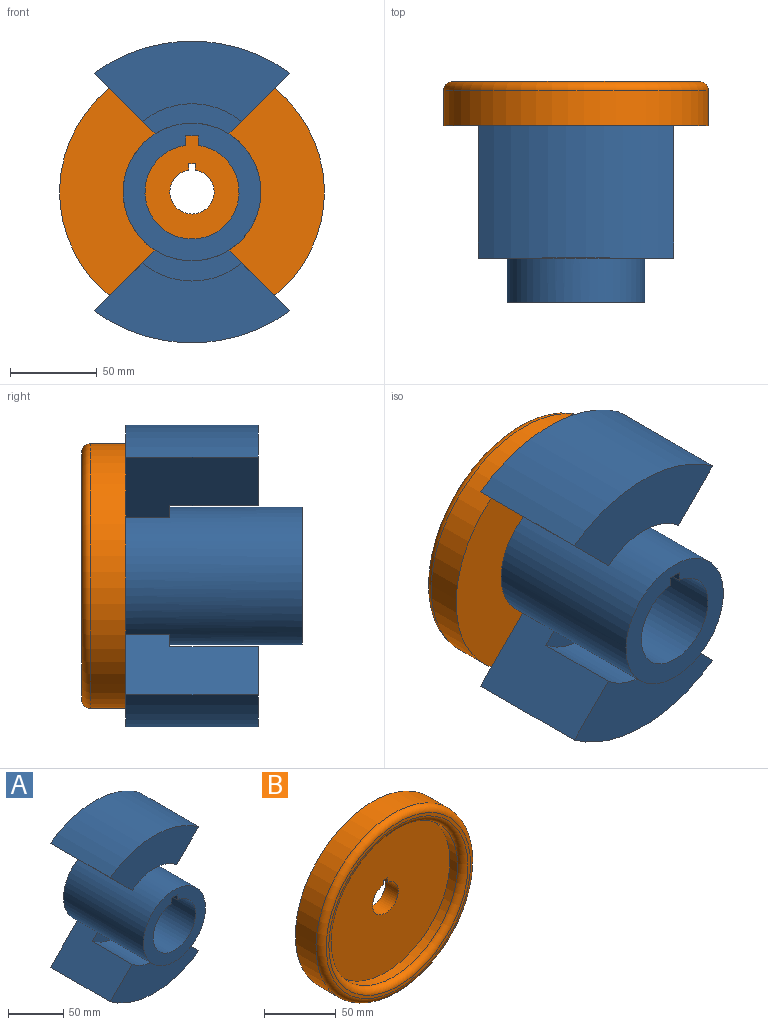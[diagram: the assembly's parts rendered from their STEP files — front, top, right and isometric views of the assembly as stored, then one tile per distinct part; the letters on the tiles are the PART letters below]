
ASSEMBLY  parts=2 mates=1
PART A: 19 faces, bbox 112.6x101.6x173.7 mm
  f0: cylinder r=39.62mm len=101.6mm, axis (0,1,0), area 23013.1mm2, adj f5,f6,f7,f8,f9,f10,f11,f12
  f1: cylinder r=27.07mm len=101.6mm, axis (0,1,0), area 16517.6mm2, adj f2,f4,f5,f6
  f2: plane 101.6x5.47mm, normal (1,0,0), area 555.6mm2, adj f1,f3,f5,f6
  f3: plane 101.6x7.47mm, normal (0,0,-1), area 758.6mm2, adj f2,f4,f5,f6
  f4: plane 101.6x5.47mm, normal (-1,0,0), area 555.6mm2, adj f1,f3,f5,f6
  f5: plane 79.25x79.25mm, normal (0,-1,0), area 2591.4mm2, adj f0,f1,f2,f3,f4
  f6: plane 173.66x112.6mm, normal (0,1,0), area 10484.5mm2, adj f0,f1,f2,f3,f4,f7,f8,f10
  f7: plane 76.2x35.02mm, normal (-0.71,0,-0.71), area 3264.3mm2, adj f0,f6,f9,f13,f14,f15
  f8: plane 76.2x35.02mm, normal (0.71,0,-0.71), area 3264.3mm2, adj f0,f6,f9,f13,f14,f15
  f9: plane 56.74x17.39mm, normal (0,-1,0), area 573mm2, adj f0,f7,f8,f13
  f10: plane 76.2x35.02mm, normal (-0.71,0,0.71), area 3242.3mm2, adj f0,f6,f12,f16,f17,f18
  f11: plane 76.2x35.02mm, normal (0.71,0,0.71), area 3242.3mm2, adj f0,f6,f12,f16,f17,f18
  f12: plane 57.36x17.82mm, normal (0,-1,0), area 599.7mm2, adj f0,f10,f11,f16
  f13: cylinder r=44.26mm len=56.74mm, axis (0,1,0), area 3129.1mm2, adj f7,f8,f9,f15
  f14: cylinder r=95.42mm len=112.6mm, axis (0,1,0), area 9176.8mm2, adj f6,f7,f8,f15
  f15: plane 112.6x46.3mm, normal (0,-1,0), area 3373.5mm2, adj f7,f8,f13,f14
  f16: cylinder r=44.69mm len=57.36mm, axis (0,1,0), area 3163.5mm2, adj f10,f11,f12,f18
  f17: cylinder r=95.42mm len=112.6mm, axis (0,1,0), area 9176.8mm2, adj f6,f10,f11,f18
  f18: plane 112.6x46mm, normal (0,-1,0), area 3346.9mm2, adj f10,f11,f16,f17
PART B: 11 faces, bbox 165x25.4x165 mm
  f0: cylinder r=63.5mm len=127mm, axis (0,1,0), area 3040.2mm2, adj f8,f9
  f1: cylinder r=76.2mm len=152.4mm, axis (0,1,0), area 9728.8mm2, adj f3,f10
  f2: plane 142.24x142.24mm, normal (0,-1,0), area 1114.8mm2, adj f9,f10
  f3: plane 152.4x152.4mm, normal (0,1,0), area 17720.6mm2, adj f1,f4,f5,f6,f7
  f4: cylinder r=12.7mm len=25.4mm, axis (0,1,0), area 964.8mm2, adj f3,f5,f7,f8
  f5: plane 12.7x3.81mm, normal (1,0,0), area 48.4mm2, adj f3,f4,f6,f8
  f6: plane 12.7x3.81mm, normal (0,0,-1), area 48.4mm2, adj f3,f5,f7,f8
  f7: plane 12.7x3.81mm, normal (-1,0,0), area 48.4mm2, adj f3,f4,f6,f8
  f8: plane 127x127mm, normal (0,-1,0), area 12146.8mm2, adj f0,f4,f5,f6,f7
  f9: torus R=68.58mm, axis (0,-1,0), area 3276.3mm2, adj f0,f2
  f10: torus R=71.12mm, axis (0,-1,0), area 3727.9mm2, adj f1,f2
PLACE A t=(-27.59,-28.02,7.15)mm
PLACE B rot(axis=(0,0,1),180deg) t=(-27.59,-28.02,7.16)mm
MATE fastened B.f3 <-> A.f1  axis (0,-1,0) through (-27.59,-28.02,7.15)mm
